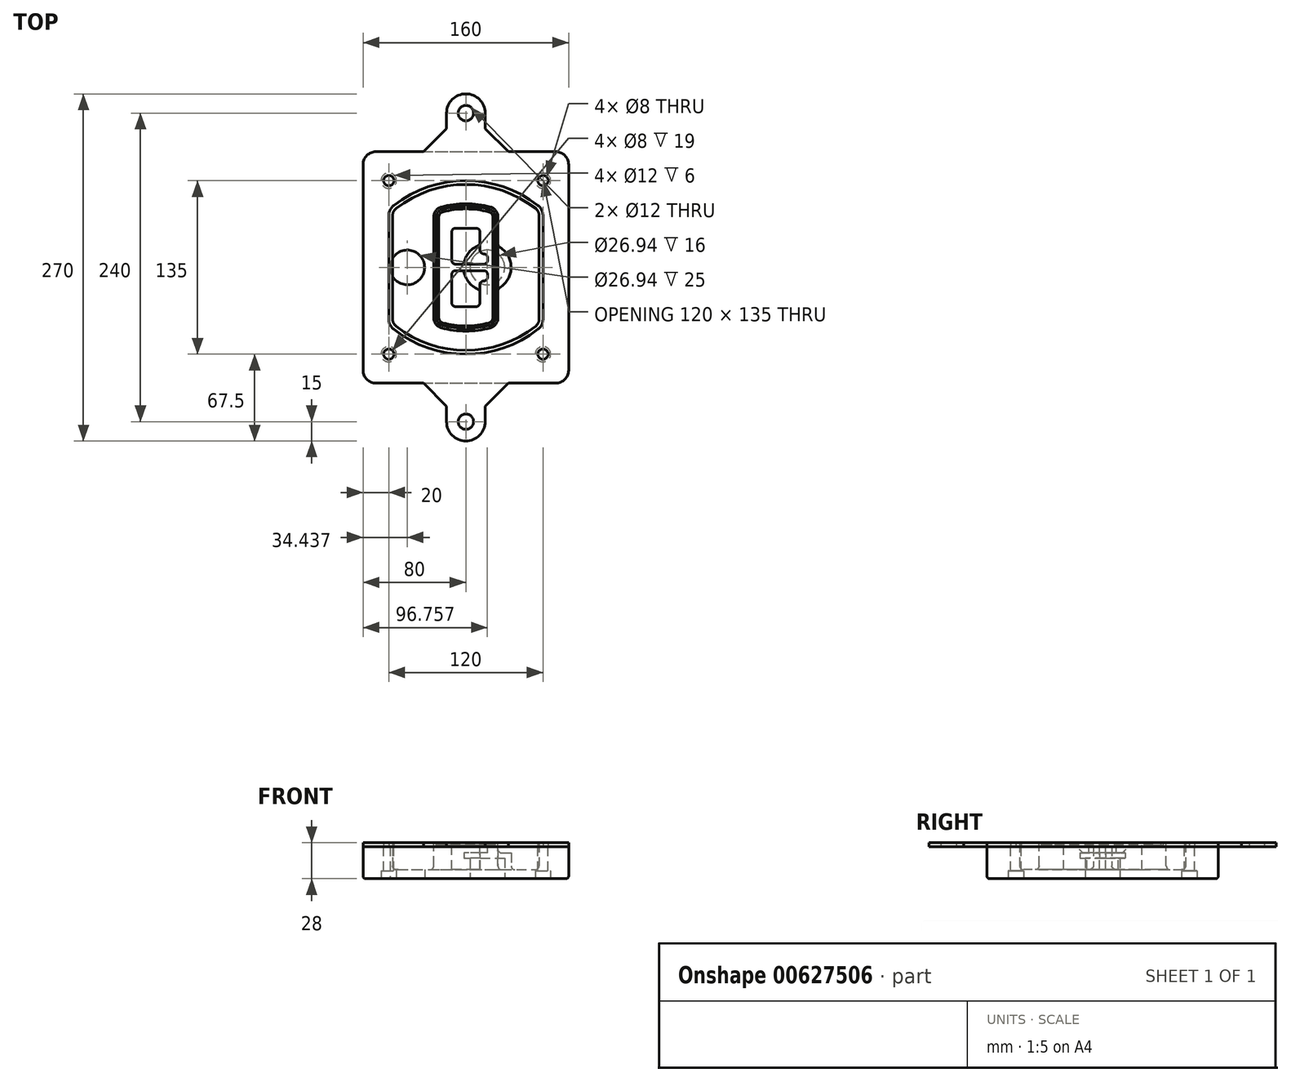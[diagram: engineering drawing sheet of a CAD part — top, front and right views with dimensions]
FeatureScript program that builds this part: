
annotation { "Feature Type Name" : "Feature", "Feature Type Description" : "" }
export const myFeature = defineFeature(function(context is Context, id is Id, definition is map)
    precondition{}
    {
        {
            var Q0;
            Q0=qCreatedBy(makeId("Top.planeOp"),FACE);
            var sketch = newSketch(context, id + "F0", { "sketchPlane" : qUnion([Q0])});
            skPoint(sketch, "E0.rect.middle", {"position": v(0, 0) * mm});
            skLineSegment(sketch, "E1.bottom", {"start": v(-70, -90) * mm, "end": v(70, -90) * mm});
            skLineSegment(sketch, "E1.top", {"start": v(-70, 90) * mm, "end": v(70, 90) * mm});
            skLineSegment(sketch, "E1.left", {"start": v(-80, -80) * mm, "end": v(-80, 80) * mm});
            skLineSegment(sketch, "E1.right", {"start": v(80, -80) * mm, "end": v(80, 80) * mm});
            skLineSegment(sketch, "E2", {"start": v(-80, 90) * mm, "end": v(80, -90) * mm, "construction": true});
            skLineSegment(sketch, "E3", {"start": v(80, 90) * mm, "end": v(-80, -90) * mm, "construction": true});
            skCircle(sketch, "E4", {"center": v(-60, 67.5) * mm, "radius": 4 * mm});
            skCircle(sketch, "E5", {"center": v(60, 67.5) * mm, "radius": 4 * mm});
            skCircle(sketch, "E6", {"center": v(60, -67.5) * mm, "radius": 4 * mm});
            skCircle(sketch, "E7", {"center": v(-60, -67.5) * mm, "radius": 4 * mm});
            skLineSegment(sketch, "E8", {"start": v(-60, 67.5) * mm, "end": v(60, 67.5) * mm, "construction": true});
            skLineSegment(sketch, "E9", {"start": v(60, 67.5) * mm, "end": v(60, -67.5) * mm, "construction": true});
            skLineSegment(sketch, "E10", {"start": v(60, -67.5) * mm, "end": v(-60, -67.5) * mm, "construction": true});
            skLineSegment(sketch, "E11", {"start": v(-60, -67.5) * mm, "end": v(-60, 67.5) * mm, "construction": true});
            skLineSegment(sketch, "E12", {"start": v(-60, 40.3) * mm, "end": v(-60, -40.3) * mm});
            skLineSegment(sketch, "E13", {"start": v(60, 40.3) * mm, "end": v(60, -40.3) * mm});
            skArc(sketch, "E14", {"start": v(56.15, 48.18) * mm, "mid": v(0, 67.5) * mm, "end": v(-56.15, 48.18) * mm});
            skArc(sketch, "E15", {"start": v(-56.15, -48.18) * mm, "mid": v(0, -67.5) * mm, "end": v(56.15, -48.18) * mm});
            skLineSegment(sketch, "E16", {"start": v(-60, 0) * mm, "end": v(60, 0) * mm, "construction": true});
            skPoint(sketch, "E17.visualSharp", {"position": v(-60, -45) * mm});
            skArc(sketch, "E17.filletArc", {"start": v(-60, -40.3) * mm, "mid": v(-58.99, -44.68) * mm, "end": v(-56.15, -48.18) * mm});
            skPoint(sketch, "E18.visualSharp", {"position": v(-60, 45) * mm});
            skArc(sketch, "E18.filletArc", {"start": v(-56.15, 48.18) * mm, "mid": v(-58.99, 44.68) * mm, "end": v(-60, 40.3) * mm});
            skPoint(sketch, "E19.visualSharp", {"position": v(60, 45) * mm});
            skArc(sketch, "E19.filletArc", {"start": v(60, 40.3) * mm, "mid": v(58.99, 44.68) * mm, "end": v(56.15, 48.18) * mm});
            skPoint(sketch, "E20.visualSharp", {"position": v(60, -45) * mm});
            skArc(sketch, "E20.filletArc", {"start": v(56.15, -48.18) * mm, "mid": v(58.99, -44.68) * mm, "end": v(60, -40.3) * mm});
            skPoint(sketch, "E21.visualSharp", {"position": v(-80, 90) * mm});
            skArc(sketch, "E21.filletArc", {"start": v(-70, 90) * mm, "mid": v(-77.07, 87.07) * mm, "end": v(-80, 80) * mm});
            skPoint(sketch, "E22.visualSharp", {"position": v(80, 90) * mm});
            skArc(sketch, "E22.filletArc", {"start": v(80, 80) * mm, "mid": v(77.07, 87.07) * mm, "end": v(70, 90) * mm});
            skPoint(sketch, "E23.visualSharp", {"position": v(80, -90) * mm});
            skArc(sketch, "E23.filletArc", {"start": v(70, -90) * mm, "mid": v(77.07, -87.07) * mm, "end": v(80, -80) * mm});
            skPoint(sketch, "E24.visualSharp", {"position": v(-80, -90) * mm});
            skArc(sketch, "E24.filletArc", {"start": v(-80, -80) * mm, "mid": v(-77.07, -87.07) * mm, "end": v(-70, -90) * mm});
            skArc(sketch, "E25.0", {"start": v(57, 40.3) * mm, "mid": v(56.3, 43.36) * mm, "end": v(54.3, 45.81) * mm});
            skLineSegment(sketch, "E25.1", {"start": v(57, 40.3) * mm, "end": v(57, -40.3) * mm});
            skArc(sketch, "E25.2", {"start": v(54.3, -45.81) * mm, "mid": v(56.3, -43.36) * mm, "end": v(57, -40.3) * mm});
            skArc(sketch, "E25.3", {"start": v(-54.3, -45.81) * mm, "mid": v(0, -64.5) * mm, "end": v(54.3, -45.81) * mm});
            skArc(sketch, "E25.4", {"start": v(-57, -40.3) * mm, "mid": v(-56.3, -43.36) * mm, "end": v(-54.3, -45.81) * mm});
            skArc(sketch, "E25.5", {"start": v(54.3, 45.81) * mm, "mid": v(0, 64.5) * mm, "end": v(-54.3, 45.81) * mm});
            skLineSegment(sketch, "E25.6", {"start": v(-57, 40.3) * mm, "end": v(-57, -40.3) * mm});
            skArc(sketch, "E25.7", {"start": v(-54.3, 45.81) * mm, "mid": v(-56.3, 43.36) * mm, "end": v(-57, 40.3) * mm});
            skArc(sketch, "E26.0", {"start": v(-58.62, 51.33) * mm, "mid": v(-62.58, 46.43) * mm, "end": v(-64, 40.3) * mm});
            skArc(sketch, "E26.1", {"start": v(58.62, 51.33) * mm, "mid": v(0, 71.5) * mm, "end": v(-58.62, 51.33) * mm});
            skArc(sketch, "E26.2", {"start": v(64, 40.3) * mm, "mid": v(62.58, 46.43) * mm, "end": v(58.62, 51.33) * mm});
            skLineSegment(sketch, "E26.3", {"start": v(64, 40.3) * mm, "end": v(64, -40.3) * mm});
            skArc(sketch, "E26.4", {"start": v(58.62, -51.33) * mm, "mid": v(62.58, -46.43) * mm, "end": v(64, -40.3) * mm});
            skLineSegment(sketch, "E26.5", {"start": v(-64, 40.3) * mm, "end": v(-64, -40.3) * mm});
            skArc(sketch, "E26.6", {"start": v(-58.62, -51.33) * mm, "mid": v(0, -71.5) * mm, "end": v(58.62, -51.33) * mm});
            skArc(sketch, "E26.7", {"start": v(-64, -40.3) * mm, "mid": v(-62.58, -46.43) * mm, "end": v(-58.62, -51.33) * mm});
            skSolve(sketch);
        }
        {
            var Q0;
            Q0=makeQuery(id+"F0.imprint","IMPRINT",FACE,{"disambiguationData":[TD([[makeQuery(id+"F0.imprint","IMPRINT",EDGE,{"derivedFrom":sQuery(id+"F0.wireOp",EDGE,"E1.bottom")}),1.0]])]});
            var Q1;
            Q1=makeQuery(id+"F0.imprint","IMPRINT",FACE,{"disambiguationData":[TD([[makeQuery(id+"F0.imprint","IMPRINT",EDGE,{"derivedFrom":sQuery(id+"F0.wireOp",EDGE,"E12")}),1.0]])]});
            var Q2;
            Q2=makeQuery(id+"F0.imprint","IMPRINT",FACE,{"disambiguationData":[TD([[makeQuery(id+"F0.imprint","IMPRINT",EDGE,{"derivedFrom":sQuery(id+"F0.wireOp",EDGE,"E25.0")}),1.0]])]});
            var Q3;
            Q3=makeQuery(id+"F0.imprint","IMPRINT",FACE,{"disambiguationData":[TD([[makeQuery(id+"F0.imprint","IMPRINT",EDGE,{"derivedFrom":sQuery(id+"F0.wireOp",EDGE,"E12")}),-1.0]])]});
            extrude(context, id + "F1", {"entities" : qUnion([Q0, Q1, Q2, Q3]), "oppositeDirection" : true, "depth" : 25 * mm});
        }
        {
            var Q0;
            Q0=makeQuery(id+"F0.imprint","IMPRINT",FACE,{"disambiguationData":[TD([[makeQuery(id+"F0.imprint","IMPRINT",EDGE,{"derivedFrom":sQuery(id+"F0.wireOp",EDGE,"E12")}),1.0]])]});
            extrude(context, id + "F2", {"entities" : qUnion([Q0]), "operationType" : NewBodyOperationType.ADD, "depth" : 3 * mm});
        }
        {
            var Q0;
            Q0=makeQuery(id+"F0.imprint","IMPRINT",FACE,{"disambiguationData":[TD([[makeQuery(id+"F0.imprint","IMPRINT",EDGE,{"derivedFrom":sQuery(id+"F0.wireOp",EDGE,"E25.0")}),1.0]])]});
            extrude(context, id + "F3", {"entities" : qUnion([Q0]), "operationType" : NewBodyOperationType.REMOVE, "oppositeDirection" : true, "depth" : 18 * mm});
        }
        {
            var Q0;
            Q0=makeQuery(id+"F2.opExtrude","CAP_FACE",FACE,{"disambiguationData":[OSD([sQuery(id+"F0.wireOp",EDGE,"E12"),sQuery(id+"F0.wireOp",EDGE,"E13"),sQuery(id+"F0.wireOp",EDGE,"E14"),sQuery(id+"F0.wireOp",EDGE,"E15"),sQuery(id+"F0.wireOp",EDGE,"E17.filletArc"),sQuery(id+"F0.wireOp",EDGE,"E18.filletArc"),sQuery(id+"F0.wireOp",EDGE,"E19.filletArc"),sQuery(id+"F0.wireOp",EDGE,"E20.filletArc"),sQuery(id+"F0.wireOp",EDGE,"E25.0"),sQuery(id+"F0.wireOp",EDGE,"E25.1"),sQuery(id+"F0.wireOp",EDGE,"E25.2"),sQuery(id+"F0.wireOp",EDGE,"E25.3"),sQuery(id+"F0.wireOp",EDGE,"E25.4"),sQuery(id+"F0.wireOp",EDGE,"E25.5"),sQuery(id+"F0.wireOp",EDGE,"E25.6"),sQuery(id+"F0.wireOp",EDGE,"E25.7")])],"isStart":false});
            var sketch = newSketch(context, id + "F4", { "sketchPlane" : qUnion([Q0])});
            skArc(sketch, "E27.0", {"start": v(-19.08, -46.97) * mm, "mid": v(0, -49.5) * mm, "end": v(19.08, -46.97) * mm});
            skArc(sketch, "E28.0", {"start": v(19.08, 46.97) * mm, "mid": v(0, 49.5) * mm, "end": v(-19.08, 46.97) * mm});
            skLineSegment(sketch, "E29", {"start": v(-25, 39.25) * mm, "end": v(-25, -39.25) * mm});
            skLineSegment(sketch, "E30", {"start": v(25, 39.25) * mm, "end": v(25, -39.25) * mm});
            skLineSegment(sketch, "E31", {"start": v(-25, 45.1) * mm, "end": v(25, 45.1) * mm, "construction": true});
            skLineSegment(sketch, "E32", {"start": v(-25, -45.1) * mm, "end": v(25, -45.1) * mm, "construction": true});
            skPoint(sketch, "E33.visualSharp", {"position": v(-25, 45.1) * mm});
            skArc(sketch, "E33.filletArc", {"start": v(-19.08, 46.97) * mm, "mid": v(-23.35, 44.11) * mm, "end": v(-25, 39.25) * mm});
            skPoint(sketch, "E34.visualSharp", {"position": v(25, 45.1) * mm});
            skArc(sketch, "E34.filletArc", {"start": v(25, 39.25) * mm, "mid": v(23.35, 44.11) * mm, "end": v(19.08, 46.97) * mm});
            skPoint(sketch, "E35.visualSharp", {"position": v(25, -45.1) * mm});
            skArc(sketch, "E35.filletArc", {"start": v(19.08, -46.97) * mm, "mid": v(23.35, -44.11) * mm, "end": v(25, -39.25) * mm});
            skPoint(sketch, "E36.visualSharp", {"position": v(-25, -45.1) * mm});
            skArc(sketch, "E36.filletArc", {"start": v(-25, -39.25) * mm, "mid": v(-23.35, -44.11) * mm, "end": v(-19.08, -46.97) * mm});
            skArc(sketch, "E37.0", {"start": v(54.3, 45.81) * mm, "mid": v(0, 64.5) * mm, "end": v(-54.3, 45.81) * mm});
            skArc(sketch, "E37.1", {"start": v(-54.3, 45.81) * mm, "mid": v(-56.3, 43.36) * mm, "end": v(-57, 40.3) * mm});
            skLineSegment(sketch, "E37.2", {"start": v(-57, 40.3) * mm, "end": v(-57, -40.3) * mm});
            skArc(sketch, "E37.3", {"start": v(-57, -40.3) * mm, "mid": v(-56.3, -43.36) * mm, "end": v(-54.3, -45.81) * mm});
            skArc(sketch, "E37.4", {"start": v(-54.3, -45.81) * mm, "mid": v(0, -64.5) * mm, "end": v(54.3, -45.81) * mm});
            skArc(sketch, "E37.5", {"start": v(54.3, -45.81) * mm, "mid": v(56.3, -43.36) * mm, "end": v(57, -40.3) * mm});
            skLineSegment(sketch, "E37.6", {"start": v(57, 40.3) * mm, "end": v(57, -40.3) * mm});
            skArc(sketch, "E37.7", {"start": v(57, 40.3) * mm, "mid": v(56.3, 43.36) * mm, "end": v(54.3, 45.81) * mm});
            skLineSegment(sketch, "E38.0", {"start": v(23, 39.25) * mm, "end": v(23, -39.25) * mm});
            skArc(sketch, "E38.1", {"start": v(18.56, -45.04) * mm, "mid": v(21.76, -42.9) * mm, "end": v(23, -39.25) * mm});
            skArc(sketch, "E38.2", {"start": v(-18.56, -45.04) * mm, "mid": v(0, -47.5) * mm, "end": v(18.56, -45.04) * mm});
            skArc(sketch, "E38.3", {"start": v(-23, -39.25) * mm, "mid": v(-21.76, -42.9) * mm, "end": v(-18.56, -45.04) * mm});
            skLineSegment(sketch, "E38.4", {"start": v(-23, 39.25) * mm, "end": v(-23, -39.25) * mm});
            skArc(sketch, "E38.5", {"start": v(23, 39.25) * mm, "mid": v(21.76, 42.9) * mm, "end": v(18.56, 45.04) * mm});
            skArc(sketch, "E38.6", {"start": v(-18.56, 45.04) * mm, "mid": v(-21.76, 42.9) * mm, "end": v(-23, 39.25) * mm});
            skArc(sketch, "E38.7", {"start": v(18.56, 45.04) * mm, "mid": v(0, 47.5) * mm, "end": v(-18.56, 45.04) * mm});
            skArc(sketch, "E39.0", {"start": v(21, 39.25) * mm, "mid": v(20.18, 41.68) * mm, "end": v(18.04, 43.1) * mm});
            skLineSegment(sketch, "E39.1", {"start": v(21, 39.25) * mm, "end": v(21, -39.25) * mm});
            skArc(sketch, "E39.2", {"start": v(18.04, -43.1) * mm, "mid": v(20.18, -41.68) * mm, "end": v(21, -39.25) * mm});
            skArc(sketch, "E39.3", {"start": v(-18.04, -43.1) * mm, "mid": v(0, -45.5) * mm, "end": v(18.04, -43.1) * mm});
            skArc(sketch, "E39.4", {"start": v(-21, -39.25) * mm, "mid": v(-20.18, -41.68) * mm, "end": v(-18.04, -43.1) * mm});
            skArc(sketch, "E39.5", {"start": v(18.04, 43.1) * mm, "mid": v(0, 45.5) * mm, "end": v(-18.04, 43.1) * mm});
            skLineSegment(sketch, "E39.6", {"start": v(-21, 39.25) * mm, "end": v(-21, -39.25) * mm});
            skArc(sketch, "E39.7", {"start": v(-18.04, 43.1) * mm, "mid": v(-20.18, 41.68) * mm, "end": v(-21, 39.25) * mm});
            skLineSegment(sketch, "E40", {"start": v(-25, 0) * mm, "end": v(25, 0) * mm, "construction": true});
            skLineSegment(sketch, "E41", {"start": v(-11, 5.5) * mm, "end": v(-11, 27.5) * mm});
            skLineSegment(sketch, "E42", {"start": v(-8, 30.5) * mm, "end": v(8, 30.5) * mm});
            skLineSegment(sketch, "E43", {"start": v(11, 27.5) * mm, "end": v(11, 13.5) * mm});
            skLineSegment(sketch, "E44", {"start": v(14, 10.5) * mm, "end": v(14, 10.5) * mm});
            skLineSegment(sketch, "E45", {"start": v(17, 7.5) * mm, "end": v(17, 5.5) * mm});
            skLineSegment(sketch, "E46", {"start": v(14, 2.5) * mm, "end": v(-8, 2.5) * mm});
            skPoint(sketch, "E47.visualSharp", {"position": v(-11, 30.5) * mm});
            skArc(sketch, "E47.filletArc", {"start": v(-8, 30.5) * mm, "mid": v(-10.12, 29.62) * mm, "end": v(-11, 27.5) * mm});
            skPoint(sketch, "E48.visualSharp", {"position": v(11, 30.5) * mm});
            skArc(sketch, "E48.filletArc", {"start": v(11, 27.5) * mm, "mid": v(10.12, 29.62) * mm, "end": v(8, 30.5) * mm});
            skPoint(sketch, "E49.visualSharp", {"position": v(11, 10.5) * mm});
            skArc(sketch, "E49.filletArc", {"start": v(11, 13.5) * mm, "mid": v(11.88, 11.38) * mm, "end": v(14, 10.5) * mm});
            skPoint(sketch, "E50.visualSharp", {"position": v(17, 10.5) * mm});
            skArc(sketch, "E50.filletArc", {"start": v(17, 7.5) * mm, "mid": v(16.12, 9.62) * mm, "end": v(14, 10.5) * mm});
            skPoint(sketch, "E51.visualSharp", {"position": v(17, 2.5) * mm});
            skArc(sketch, "E51.filletArc", {"start": v(14, 2.5) * mm, "mid": v(16.12, 3.38) * mm, "end": v(17, 5.5) * mm});
            skPoint(sketch, "E52.visualSharp", {"position": v(-11, 2.5) * mm});
            skArc(sketch, "E52.filletArc", {"start": v(-11, 5.5) * mm, "mid": v(-10.12, 3.38) * mm, "end": v(-8, 2.5) * mm});
            skLineSegment(sketch, "E53.0.MirrorCS", {"start": v(14, -2.5) * mm, "end": v(-8, -2.5) * mm});
            skArc(sketch, "E54.0.MirrorCS", {"start": v(-11, -5.5) * mm, "mid": v(-10.12, -3.38) * mm, "end": v(-8, -2.5) * mm});
            skLineSegment(sketch, "E55.0.MirrorCS", {"start": v(-11, -5.5) * mm, "end": v(-11, -27.5) * mm});
            skArc(sketch, "E56.0.MirrorCS", {"start": v(-8, -30.5) * mm, "mid": v(-10.12, -29.62) * mm, "end": v(-11, -27.5) * mm});
            skLineSegment(sketch, "E57.0.MirrorCS", {"start": v(-8, -30.5) * mm, "end": v(8, -30.5) * mm});
            skArc(sketch, "E58.0.MirrorCS", {"start": v(11, -27.5) * mm, "mid": v(10.12, -29.62) * mm, "end": v(8, -30.5) * mm});
            skLineSegment(sketch, "E59.0.MirrorCS", {"start": v(11, -27.5) * mm, "end": v(11, -13.5) * mm});
            skArc(sketch, "E60.0.MirrorCS", {"start": v(11, -13.5) * mm, "mid": v(11.88, -11.38) * mm, "end": v(14, -10.5) * mm});
            skArc(sketch, "E61.0.MirrorCS", {"start": v(17, -7.5) * mm, "mid": v(16.12, -9.62) * mm, "end": v(14, -10.5) * mm});
            skLineSegment(sketch, "E62.0.MirrorCS", {"start": v(17, -7.5) * mm, "end": v(17, -5.5) * mm});
            skArc(sketch, "E63.0.MirrorCS", {"start": v(14, -2.5) * mm, "mid": v(16.12, -3.38) * mm, "end": v(17, -5.5) * mm});
            skSolve(sketch);
        }
        {
            var Q0;
            Q0=makeQuery(id+"F4.imprint","IMPRINT",FACE,{"disambiguationData":[TD([[makeQuery(id+"F4.imprint","IMPRINT",EDGE,{"derivedFrom":sQuery(id+"F4.wireOp",EDGE,"E27.0")}),1.0]])]});
            var Q1;
            Q1=makeQuery(id+"F4.imprint","IMPRINT",FACE,{"disambiguationData":[TD([[makeQuery(id+"F4.imprint","IMPRINT",EDGE,{"derivedFrom":sQuery(id+"F4.wireOp",EDGE,"E38.0")}),-1.0]])]});
            var Q2;
            Q2=makeQuery(id+"F4.imprint","IMPRINT",FACE,{"disambiguationData":[TD([[makeQuery(id+"F4.imprint","IMPRINT",EDGE,{"derivedFrom":sQuery(id+"F4.wireOp",EDGE,"E39.0")}),1.0]])]});
            extrude(context, id + "F5", {"entities" : qUnion([Q0, Q1, Q2]), "operationType" : NewBodyOperationType.ADD, "endBound" : BoundingType.UP_TO_NEXT, "oppositeDirection" : true, "depth" : 25 * mm});
        }
        {
            var Q0;
            Q0=makeQuery(id+"F4.imprint","IMPRINT",FACE,{"disambiguationData":[TD([[makeQuery(id+"F4.imprint","IMPRINT",EDGE,{"derivedFrom":sQuery(id+"F4.wireOp",EDGE,"E38.0")}),-1.0]])]});
            extrude(context, id + "F6", {"entities" : qUnion([Q0]), "operationType" : NewBodyOperationType.REMOVE, "oppositeDirection" : true, "depth" : 2 * mm});
        }
        {
            var Q0;
            Q0=makeQuery(id+"F1.opExtrude","CAP_FACE",FACE,{"disambiguationData":[OSD([sQuery(id+"F0.wireOp",EDGE,"E1.bottom"),sQuery(id+"F0.wireOp",EDGE,"E1.top"),sQuery(id+"F0.wireOp",EDGE,"E1.left"),sQuery(id+"F0.wireOp",EDGE,"E1.right"),sQuery(id+"F0.wireOp",EDGE,"E4"),sQuery(id+"F0.wireOp",EDGE,"E5"),sQuery(id+"F0.wireOp",EDGE,"E6"),sQuery(id+"F0.wireOp",EDGE,"E7"),sQuery(id+"F0.wireOp",EDGE,"E21.filletArc"),sQuery(id+"F0.wireOp",EDGE,"E22.filletArc"),sQuery(id+"F0.wireOp",EDGE,"E23.filletArc"),sQuery(id+"F0.wireOp",EDGE,"E24.filletArc")])],"isStart":false});
            var sketch = newSketch(context, id + "F7", { "sketchPlane" : qUnion([Q0])});
            skCircle(sketch, "E64", {"center": v(16.76, 0) * mm, "radius": 13.47 * mm});
            skCircle(sketch, "E65", {"center": v(-45.56, 0) * mm, "radius": 13.47 * mm});
            skLineSegment(sketch, "E66", {"start": v(80, 0) * mm, "end": v(-80, 0) * mm});
            skCircle(sketch, "E67", {"center": v(16.76, 0) * mm, "radius": 18.47 * mm});
            skCircle(sketch, "E68", {"center": v(60, -67.5) * mm, "radius": 6 * mm});
            skCircle(sketch, "E69", {"center": v(-60, -67.5) * mm, "radius": 6 * mm});
            skCircle(sketch, "E70", {"center": v(-60, 67.5) * mm, "radius": 6 * mm});
            skCircle(sketch, "E71", {"center": v(60, 67.5) * mm, "radius": 6 * mm});
            skSolve(sketch);
        }
        {
            var Q0;
            {var subQ1=sQuery(id+"F7.wireOp",EDGE,"E66");var subQ4=sQuery(id+"F7.wireOp",EDGE,"E64");var subQ6=makeQuery(id+"F7.imprint","INTERSECT",VERTEX,{"disambiguationData":[OD(0.0)],"derivedFrom":[subQ4,subQ1]});Q0=makeQuery(id+"F7.imprint","IMPRINT",FACE,{"disambiguationData":[TD([[makeQuery(id+"F7.imprint","IMPRINT",EDGE,{"disambiguationData":[TD([[subQ6,-1.0]])],"derivedFrom":subQ4}),-1.0]])]});}
            var Q1;
            {var subQ0=sQuery(id+"F7.wireOp",EDGE,"E66");var subQ1=sQuery(id+"F7.wireOp",EDGE,"E64");var subQ3=makeQuery(id+"F7.imprint","INTERSECT",VERTEX,{"disambiguationData":[OD(0.0)],"derivedFrom":[subQ1,subQ0]});Q1=makeQuery(id+"F7.imprint","IMPRINT",FACE,{"disambiguationData":[TD([[makeQuery(id+"F7.imprint","IMPRINT",EDGE,{"disambiguationData":[TD([[subQ3,-1.0]])],"derivedFrom":subQ1}),1.0]])]});}
            var Q2;
            {var subQ0=sQuery(id+"F7.wireOp",EDGE,"E66");var subQ1=sQuery(id+"F7.wireOp",EDGE,"E64");var subQ3=makeQuery(id+"F7.imprint","INTERSECT",VERTEX,{"disambiguationData":[OD(0.0)],"derivedFrom":[subQ1,subQ0]});Q2=makeQuery(id+"F7.imprint","IMPRINT",FACE,{"disambiguationData":[TD([[makeQuery(id+"F7.imprint","IMPRINT",EDGE,{"disambiguationData":[TD([[subQ3,1.0]])],"derivedFrom":subQ1}),1.0]])]});}
            var Q3;
            {var subQ1=sQuery(id+"F7.wireOp",EDGE,"E66");var subQ4=sQuery(id+"F7.wireOp",EDGE,"E64");var subQ6=makeQuery(id+"F7.imprint","INTERSECT",VERTEX,{"disambiguationData":[OD(0.0)],"derivedFrom":[subQ4,subQ1]});Q3=makeQuery(id+"F7.imprint","IMPRINT",FACE,{"disambiguationData":[TD([[makeQuery(id+"F7.imprint","IMPRINT",EDGE,{"disambiguationData":[TD([[subQ6,1.0]])],"derivedFrom":subQ4}),-1.0]])]});}
            extrude(context, id + "F8", {"entities" : qUnion([Q0, Q1, Q2, Q3]), "operationType" : NewBodyOperationType.ADD, "oppositeDirection" : true, "depth" : 20 * mm});
        }
        {
            var Q0;
            {var subQ0=sQuery(id+"F7.wireOp",EDGE,"E66");var subQ1=sQuery(id+"F7.wireOp",EDGE,"E64");var subQ3=makeQuery(id+"F7.imprint","INTERSECT",VERTEX,{"disambiguationData":[OD(0.0)],"derivedFrom":[subQ1,subQ0]});Q0=makeQuery(id+"F7.imprint","IMPRINT",FACE,{"disambiguationData":[TD([[makeQuery(id+"F7.imprint","IMPRINT",EDGE,{"disambiguationData":[TD([[subQ3,-1.0]])],"derivedFrom":subQ1}),1.0]])]});}
            var Q1;
            {var subQ0=sQuery(id+"F7.wireOp",EDGE,"E66");var subQ1=sQuery(id+"F7.wireOp",EDGE,"E64");var subQ3=makeQuery(id+"F7.imprint","INTERSECT",VERTEX,{"disambiguationData":[OD(0.0)],"derivedFrom":[subQ1,subQ0]});Q1=makeQuery(id+"F7.imprint","IMPRINT",FACE,{"disambiguationData":[TD([[makeQuery(id+"F7.imprint","IMPRINT",EDGE,{"disambiguationData":[TD([[subQ3,1.0]])],"derivedFrom":subQ1}),1.0]])]});}
            extrude(context, id + "F9", {"entities" : qUnion([Q0, Q1]), "operationType" : NewBodyOperationType.REMOVE, "oppositeDirection" : true, "depth" : 16 * mm});
        }
        {
            var Q0;
            {var subQ0=sQuery(id+"F7.wireOp",EDGE,"E66");var subQ1=sQuery(id+"F7.wireOp",EDGE,"E65");var subQ3=makeQuery(id+"F7.imprint","INTERSECT",VERTEX,{"disambiguationData":[OD(0.0)],"derivedFrom":[subQ1,subQ0]});Q0=makeQuery(id+"F7.imprint","IMPRINT",FACE,{"disambiguationData":[TD([[makeQuery(id+"F7.imprint","IMPRINT",EDGE,{"disambiguationData":[TD([[subQ3,-1.0]])],"derivedFrom":subQ1}),1.0]])]});}
            var Q1;
            {var subQ0=sQuery(id+"F7.wireOp",EDGE,"E66");var subQ1=sQuery(id+"F7.wireOp",EDGE,"E65");var subQ3=makeQuery(id+"F7.imprint","INTERSECT",VERTEX,{"disambiguationData":[OD(0.0)],"derivedFrom":[subQ1,subQ0]});Q1=makeQuery(id+"F7.imprint","IMPRINT",FACE,{"disambiguationData":[TD([[makeQuery(id+"F7.imprint","IMPRINT",EDGE,{"disambiguationData":[TD([[subQ3,1.0]])],"derivedFrom":subQ1}),1.0]])]});}
            extrude(context, id + "F10", {"entities" : qUnion([Q0, Q1]), "operationType" : NewBodyOperationType.REMOVE, "oppositeDirection" : true, "depth" : 25 * mm});
        }
        {
            var Q0;
            Q0=makeQuery(id+"F7.imprint","IMPRINT",FACE,{"disambiguationData":[TD([[makeQuery(id+"F7.imprint","IMPRINT",EDGE,{"derivedFrom":sQuery(id+"F7.wireOp",EDGE,"E68")}),1.0]])]});
            var Q1;
            Q1=makeQuery(id+"F7.imprint","IMPRINT",FACE,{"disambiguationData":[TD([[makeQuery(id+"F7.imprint","IMPRINT",EDGE,{"derivedFrom":makeQuery(id+"F1.opExtrude","CAP_EDGE",EDGE,{"disambiguationData":[OSD([sQuery(id+"F0.wireOp",EDGE,"E5")])],"isStart":false})}),-1.0]])]});
            var Q2;
            Q2=makeQuery(id+"F7.imprint","IMPRINT",FACE,{"disambiguationData":[TD([[makeQuery(id+"F7.imprint","IMPRINT",EDGE,{"derivedFrom":sQuery(id+"F7.wireOp",EDGE,"E69")}),1.0]])]});
            var Q3;
            Q3=makeQuery(id+"F7.imprint","IMPRINT",FACE,{"disambiguationData":[TD([[makeQuery(id+"F7.imprint","IMPRINT",EDGE,{"derivedFrom":makeQuery(id+"F1.opExtrude","CAP_EDGE",EDGE,{"disambiguationData":[OSD([sQuery(id+"F0.wireOp",EDGE,"E4")])],"isStart":false})}),-1.0]])]});
            var Q4;
            Q4=makeQuery(id+"F7.imprint","IMPRINT",FACE,{"disambiguationData":[TD([[makeQuery(id+"F7.imprint","IMPRINT",EDGE,{"derivedFrom":sQuery(id+"F7.wireOp",EDGE,"E70")}),1.0]])]});
            var Q5;
            Q5=makeQuery(id+"F7.imprint","IMPRINT",FACE,{"disambiguationData":[TD([[makeQuery(id+"F7.imprint","IMPRINT",EDGE,{"derivedFrom":makeQuery(id+"F1.opExtrude","CAP_EDGE",EDGE,{"disambiguationData":[OSD([sQuery(id+"F0.wireOp",EDGE,"E7")])],"isStart":false})}),-1.0]])]});
            var Q6;
            Q6=makeQuery(id+"F7.imprint","IMPRINT",FACE,{"disambiguationData":[TD([[makeQuery(id+"F7.imprint","IMPRINT",EDGE,{"derivedFrom":sQuery(id+"F7.wireOp",EDGE,"E71")}),1.0]])]});
            var Q7;
            Q7=makeQuery(id+"F7.imprint","IMPRINT",FACE,{"disambiguationData":[TD([[makeQuery(id+"F7.imprint","IMPRINT",EDGE,{"derivedFrom":makeQuery(id+"F1.opExtrude","CAP_EDGE",EDGE,{"disambiguationData":[OSD([sQuery(id+"F0.wireOp",EDGE,"E6")])],"isStart":false})}),-1.0]])]});
            extrude(context, id + "F11", {"entities" : qUnion([Q0, Q1, Q2, Q3, Q4, Q5, Q6, Q7]), "operationType" : NewBodyOperationType.REMOVE, "oppositeDirection" : true, "depth" : 6 * mm});
        }
        {
            var Q0;
            Q0=makeQuery(id+"F9.boolean.opBoolean","COPY",FACE,{"derivedFrom":makeQuery(id+"F9.opExtrude","CAP_FACE",FACE,{"disambiguationData":[OSD([sQuery(id+"F7.wireOp",EDGE,"E64")])],"isStart":false})});
            var sketch = newSketch(context, id + "F12", { "sketchPlane" : qUnion([Q0])});
            skArc(sketch, "E72.0", {"start": v(11, 17.55) * mm, "mid": v(2.57, 11.82) * mm, "end": v(-1.54, 2.5) * mm});
            skArc(sketch, "E72.1", {"start": v(-1.54, -2.5) * mm, "mid": v(2.57, -11.82) * mm, "end": v(11, -17.55) * mm});
            skLineSegment(sketch, "E73", {"start": v(-1.54, -2.5) * mm, "end": v(14, -2.5) * mm});
            skLineSegment(sketch, "E74.0", {"start": v(14, 2.5) * mm, "end": v(-1.54, 2.5) * mm});
            skArc(sketch, "E74.1", {"start": v(14, 2.5) * mm, "mid": v(16.12, 3.38) * mm, "end": v(17, 5.5) * mm});
            skLineSegment(sketch, "E74.2", {"start": v(17, 7.5) * mm, "end": v(17, 5.5) * mm});
            skArc(sketch, "E74.3", {"start": v(17, 7.5) * mm, "mid": v(16.12, 9.62) * mm, "end": v(14, 10.5) * mm});
            skArc(sketch, "E74.4", {"start": v(11, 13.5) * mm, "mid": v(11.88, 11.38) * mm, "end": v(14, 10.5) * mm});
            skLineSegment(sketch, "E74.5", {"start": v(11, 17.55) * mm, "end": v(11, 13.5) * mm});
            skLineSegment(sketch, "E74.7", {"start": v(14, -2.5) * mm, "end": v(-1.54, -2.5) * mm});
            skArc(sketch, "E74.8", {"start": v(14, -2.5) * mm, "mid": v(16.12, -3.38) * mm, "end": v(17, -5.5) * mm});
            skLineSegment(sketch, "E74.9", {"start": v(17, -7.5) * mm, "end": v(17, -5.5) * mm});
            skArc(sketch, "E74.10", {"start": v(17, -7.5) * mm, "mid": v(16.12, -9.62) * mm, "end": v(14, -10.5) * mm});
            skArc(sketch, "E74.11", {"start": v(11, -13.5) * mm, "mid": v(11.88, -11.38) * mm, "end": v(14, -10.5) * mm});
            skLineSegment(sketch, "E74.12", {"start": v(11, -17.55) * mm, "end": v(11, -13.5) * mm});
            skPoint(sketch, "E75.orphan", {"position": v(11, -27.5) * mm});
            skPoint(sketch, "E76.orphan", {"position": v(-8, -2.5) * mm});
            skPoint(sketch, "E77.orphan", {"position": v(-8, 2.5) * mm});
            skPoint(sketch, "E78.orphan", {"position": v(11, 27.5) * mm});
            skSolve(sketch);
        }
        {
            var Q0;
            {var subQ7=sQuery(id+"F12.wireOp",EDGE,"E72.0");var subQ14=sQuery(id+"F12.wireOp",EDGE,"E72.1");var subQ16=sQuery(id+"F12.wireOp",EDGE,"E74.1");var subQ18=sQuery(id+"F12.wireOp",EDGE,"E74.8");Q0=qUnion([makeQuery(id+"F12.imprint","IMPRINT",FACE,{"disambiguationData":[TD([[makeQuery(id+"F12.imprint","IMPRINT",EDGE,{"derivedFrom":subQ7}),1.0]])]}),makeQuery(id+"F12.imprint","IMPRINT",FACE,{"disambiguationData":[TD([[makeQuery(id+"F12.imprint","IMPRINT",EDGE,{"derivedFrom":subQ14}),1.0]])]}),makeQuery(id+"F12.imprint","IMPRINT",FACE,{"disambiguationData":[TD([[makeQuery(id+"F12.imprint","IMPRINT",EDGE,{"derivedFrom":subQ16}),1.0]])]}),makeQuery(id+"F12.imprint","IMPRINT",FACE,{"disambiguationData":[TD([[makeQuery(id+"F12.imprint","IMPRINT",EDGE,{"derivedFrom":subQ18}),-1.0]])]})]);}
            var Q1;
            Q1=makeQuery(id+"F5.boolean.opBoolean","SPLIT",FACE,{"disambiguationData":[TD([makeQuery(id+"F5.opExtrude","SWEPT_FACE",FACE,{"disambiguationData":[OSD([sQuery(id+"F4.wireOp",EDGE,"E41")])]})])],"derivedFrom":makeQuery(id+"F3.boolean.opBoolean","COPY",FACE,{"derivedFrom":makeQuery(id+"F3.opExtrude","CAP_FACE",FACE,{"disambiguationData":[OSD([sQuery(id+"F0.wireOp",EDGE,"E25.0"),sQuery(id+"F0.wireOp",EDGE,"E25.1"),sQuery(id+"F0.wireOp",EDGE,"E25.2"),sQuery(id+"F0.wireOp",EDGE,"E25.3"),sQuery(id+"F0.wireOp",EDGE,"E25.4"),sQuery(id+"F0.wireOp",EDGE,"E25.5"),sQuery(id+"F0.wireOp",EDGE,"E25.6"),sQuery(id+"F0.wireOp",EDGE,"E25.7")])],"isStart":false})})});
            extrude(context, id + "F13", {"entities" : qUnion([Q0]), "operationType" : NewBodyOperationType.REMOVE, "endBound" : BoundingType.UP_TO_SURFACE, "endBoundEntityFace" : qUnion([Q1]), "depth" : 25 * mm});
        }
        {
            var Q0;
            Q0=makeQuery(id+"F3.boolean.opBoolean","COPY",EDGE,{"derivedFrom":makeQuery(id+"F3.opExtrude","CAP_EDGE",EDGE,{"disambiguationData":[OSD([sQuery(id+"F0.wireOp",EDGE,"E25.6")])],"isStart":false})});
            var Q1;
            Q1=makeQuery(id+"F8.boolean.opBoolean","INTERSECT",EDGE,{"derivedFrom":[makeQuery(id+"F5.opExtrude","SWEPT_FACE",FACE,{"disambiguationData":[OSD([sQuery(id+"F4.wireOp",EDGE,"E30")])]}),makeQuery(id+"F8.opExtrude","CAP_FACE",FACE,{"disambiguationData":[OSD([sQuery(id+"F7.wireOp",EDGE,"E67")])],"isStart":false})]});
            var Q2;
            Q2=makeQuery(id+"F8.boolean.opBoolean","INTERSECT",EDGE,{"disambiguationData":[OD(1.0)],"derivedFrom":[makeQuery(id+"F5.opExtrude","SWEPT_FACE",FACE,{"disambiguationData":[OSD([sQuery(id+"F4.wireOp",EDGE,"E30")])]}),makeQuery(id+"F8.opExtrude","SWEPT_FACE",FACE,{"disambiguationData":[OSD([sQuery(id+"F7.wireOp",EDGE,"E67")])]})]});
            var Q3;
            {var subQ0=sQuery(id+"F4.wireOp",EDGE,"E30");Q3=makeQuery(id+"F8.boolean.opBoolean","SPLIT",EDGE,{"disambiguationData":[TD([makeQuery(id+"F5.opExtrude","SWEPT_FACE",FACE,{"disambiguationData":[OSD([sQuery(id+"F4.wireOp",EDGE,"E35.filletArc")])]})])],"derivedFrom":makeQuery(id+"F5.opExtrude","CAP_EDGE",EDGE,{"disambiguationData":[OSD([subQ0])],"isStart":false})});}
            var Q4;
            {var subQ0=sQuery(id+"F0.wireOp",EDGE,"E25.7");var subQ1=sQuery(id+"F0.wireOp",EDGE,"E25.1");var subQ2=sQuery(id+"F0.wireOp",EDGE,"E25.6");var subQ3=sQuery(id+"F0.wireOp",EDGE,"E25.5");var subQ4=sQuery(id+"F0.wireOp",EDGE,"E25.4");var subQ5=sQuery(id+"F0.wireOp",EDGE,"E25.0");var subQ6=sQuery(id+"F0.wireOp",EDGE,"E25.2");var subQ7=sQuery(id+"F0.wireOp",EDGE,"E25.3");Q4=makeQuery(id+"F8.boolean.opBoolean","INTERSECT",EDGE,{"derivedFrom":[makeQuery(id+"F5.boolean.opBoolean","SPLIT",FACE,{"disambiguationData":[TD([makeQuery(id+"F2.opExtrude","SWEPT_FACE",FACE,{"disambiguationData":[OSD([subQ5])]})])],"derivedFrom":makeQuery(id+"F3.boolean.opBoolean","COPY",FACE,{"derivedFrom":makeQuery(id+"F3.opExtrude","CAP_FACE",FACE,{"disambiguationData":[OSD([subQ5,subQ1,subQ6,subQ7,subQ4,subQ3,subQ2,subQ0])],"isStart":false})})}),makeQuery(id+"F8.opExtrude","SWEPT_FACE",FACE,{"disambiguationData":[OSD([sQuery(id+"F7.wireOp",EDGE,"E67")])]})]});}
            var Q5;
            Q5=makeQuery(id+"F8.boolean.opBoolean","INTERSECT",EDGE,{"disambiguationData":[OD(0.0)],"derivedFrom":[makeQuery(id+"F5.opExtrude","SWEPT_FACE",FACE,{"disambiguationData":[OSD([sQuery(id+"F4.wireOp",EDGE,"E30")])]}),makeQuery(id+"F8.opExtrude","SWEPT_FACE",FACE,{"disambiguationData":[OSD([sQuery(id+"F7.wireOp",EDGE,"E67")])]})]});
            fillet(context, id + "F14", {"entities" : qUnion([Q0, Q1, Q2, Q3, Q4, Q5]), "radius" : 3 * mm, "tangentPropagation" : true, "allowEdgeOverflow" : false});
        }
        {
            var Q0;
            Q0=makeQuery(id+"F1.opExtrude","CAP_EDGE",EDGE,{"disambiguationData":[OSD([sQuery(id+"F0.wireOp",EDGE,"E1.bottom")])],"isStart":false});
            fillet(context, id + "F15", {"entities" : qUnion([Q0]), "radius" : 2 * mm, "tangentPropagation" : true, "allowEdgeOverflow" : false});
        }
        {
            var Q0;
            {var subQ0=sQuery(id+"F0.wireOp",EDGE,"E21.filletArc");var subQ1=sQuery(id+"F0.wireOp",EDGE,"E7");var subQ2=sQuery(id+"F0.wireOp",EDGE,"E6");var subQ3=sQuery(id+"F0.wireOp",EDGE,"E5");var subQ4=sQuery(id+"F0.wireOp",EDGE,"E4");var subQ5=sQuery(id+"F0.wireOp",EDGE,"E22.filletArc");var subQ6=sQuery(id+"F0.wireOp",EDGE,"E1.bottom");var subQ7=sQuery(id+"F0.wireOp",EDGE,"E1.right");var subQ8=sQuery(id+"F0.wireOp",EDGE,"E1.top");var subQ9=sQuery(id+"F0.wireOp",EDGE,"E1.left");var subQ10=sQuery(id+"F0.wireOp",EDGE,"E23.filletArc");var subQ11=sQuery(id+"F0.wireOp",EDGE,"E24.filletArc");Q0=makeQuery(id+"F2.boolean.opBoolean","SPLIT",FACE,{"disambiguationData":[TD([makeQuery(id+"F1.opExtrude","SWEPT_FACE",FACE,{"disambiguationData":[OSD([subQ6])]})])],"derivedFrom":makeQuery(id+"F1.opExtrude","CAP_FACE",FACE,{"disambiguationData":[OSD([subQ6,subQ8,subQ9,subQ7,subQ4,subQ3,subQ2,subQ1,subQ0,subQ5,subQ10,subQ11])],"isStart":true})});}
            var sketch = newSketch(context, id + "F16", { "sketchPlane" : qUnion([Q0])});
            skArc(sketch, "E79", {"start": v(15, 120) * mm, "mid": v(0, 135) * mm, "end": v(-15, 120) * mm});
            skLineSegment(sketch, "E80", {"start": v(-15, 120) * mm, "end": v(-15, 108) * mm});
            skLineSegment(sketch, "E81", {"start": v(-15, 108) * mm, "end": v(-33, 90) * mm});
            skLineSegment(sketch, "E82", {"start": v(15, 120) * mm, "end": v(15, 108) * mm});
            skLineSegment(sketch, "E83", {"start": v(15, 108) * mm, "end": v(33, 90) * mm});
            skCircle(sketch, "E84", {"center": v(0, 120) * mm, "radius": 6 * mm});
            skPoint(sketch, "E85.orphan", {"position": v(0, 90) * mm});
            skLineSegment(sketch, "E86", {"start": v(0, 90) * mm, "end": v(0, 120) * mm, "construction": true});
            skLineSegment(sketch, "E87", {"start": v(0, 0) * mm, "end": v(-80, 0) * mm, "construction": true});
            skLineSegment(sketch, "E88.MirrorCS", {"start": v(-15, -108) * mm, "end": v(-33, -90) * mm});
            skLineSegment(sketch, "E89.MirrorCS", {"start": v(-15, -120) * mm, "end": v(-15, -108) * mm});
            skArc(sketch, "E90.MirrorCS", {"start": v(15, -120) * mm, "mid": v(0, -135) * mm, "end": v(-15, -120) * mm});
            skCircle(sketch, "E91.MirrorC", {"center": v(0, -120) * mm, "radius": 6 * mm});
            skLineSegment(sketch, "E92.MirrorCS", {"start": v(15, -108) * mm, "end": v(33, -90) * mm});
            skLineSegment(sketch, "E93", {"start": v(15, -108) * mm, "end": v(15, -120) * mm});
            skLineSegment(sketch, "E94", {"start": v(0, -120) * mm, "end": v(0, 0) * mm, "construction": true});
            skSolve(sketch);
        }
        {
            var Q0;
            {var subQ0=sQuery(id+"F16.wireOp",EDGE,"E88.MirrorCS");Q0=makeQuery(id+"F16.imprint","IMPRINT",FACE,{"disambiguationData":[TD([[makeQuery(id+"F16.imprint","IMPRINT",EDGE,{"derivedFrom":subQ0}),-1.0]])]});}
            var Q1;
            Q1=makeQuery(id+"F16.imprint","IMPRINT",FACE,{"disambiguationData":[TD([[makeQuery(id+"F16.imprint","IMPRINT",EDGE,{"derivedFrom":makeQuery(id+"F1.opExtrude","CAP_EDGE",EDGE,{"disambiguationData":[OSD([sQuery(id+"F0.wireOp",EDGE,"E1.left")])],"isStart":true})}),-1.0]])]});
            var Q2;
            Q2=makeQuery(id+"F16.imprint","IMPRINT",FACE,{"disambiguationData":[TD([[makeQuery(id+"F16.imprint","IMPRINT",EDGE,{"derivedFrom":sQuery(id+"F16.wireOp",EDGE,"E79")}),1.0]])]});
            var Q3;
            Q3=makeQuery(id+"F2.opExtrude","CAP_FACE",FACE,{"disambiguationData":[OSD([sQuery(id+"F0.wireOp",EDGE,"E12"),sQuery(id+"F0.wireOp",EDGE,"E13"),sQuery(id+"F0.wireOp",EDGE,"E14"),sQuery(id+"F0.wireOp",EDGE,"E15"),sQuery(id+"F0.wireOp",EDGE,"E17.filletArc"),sQuery(id+"F0.wireOp",EDGE,"E18.filletArc"),sQuery(id+"F0.wireOp",EDGE,"E19.filletArc"),sQuery(id+"F0.wireOp",EDGE,"E20.filletArc"),sQuery(id+"F0.wireOp",EDGE,"E25.0"),sQuery(id+"F0.wireOp",EDGE,"E25.1"),sQuery(id+"F0.wireOp",EDGE,"E25.2"),sQuery(id+"F0.wireOp",EDGE,"E25.3"),sQuery(id+"F0.wireOp",EDGE,"E25.4"),sQuery(id+"F0.wireOp",EDGE,"E25.5"),sQuery(id+"F0.wireOp",EDGE,"E25.6"),sQuery(id+"F0.wireOp",EDGE,"E25.7")])],"isStart":false});
            extrude(context, id + "F17", {"entities" : qUnion([Q0, Q1, Q2]), "endBound" : BoundingType.UP_TO_SURFACE, "depth" : 25 * mm, "endBoundEntityFace" : qUnion([Q3]), "offsetDistance" : 25 * mm});
        }
    });
